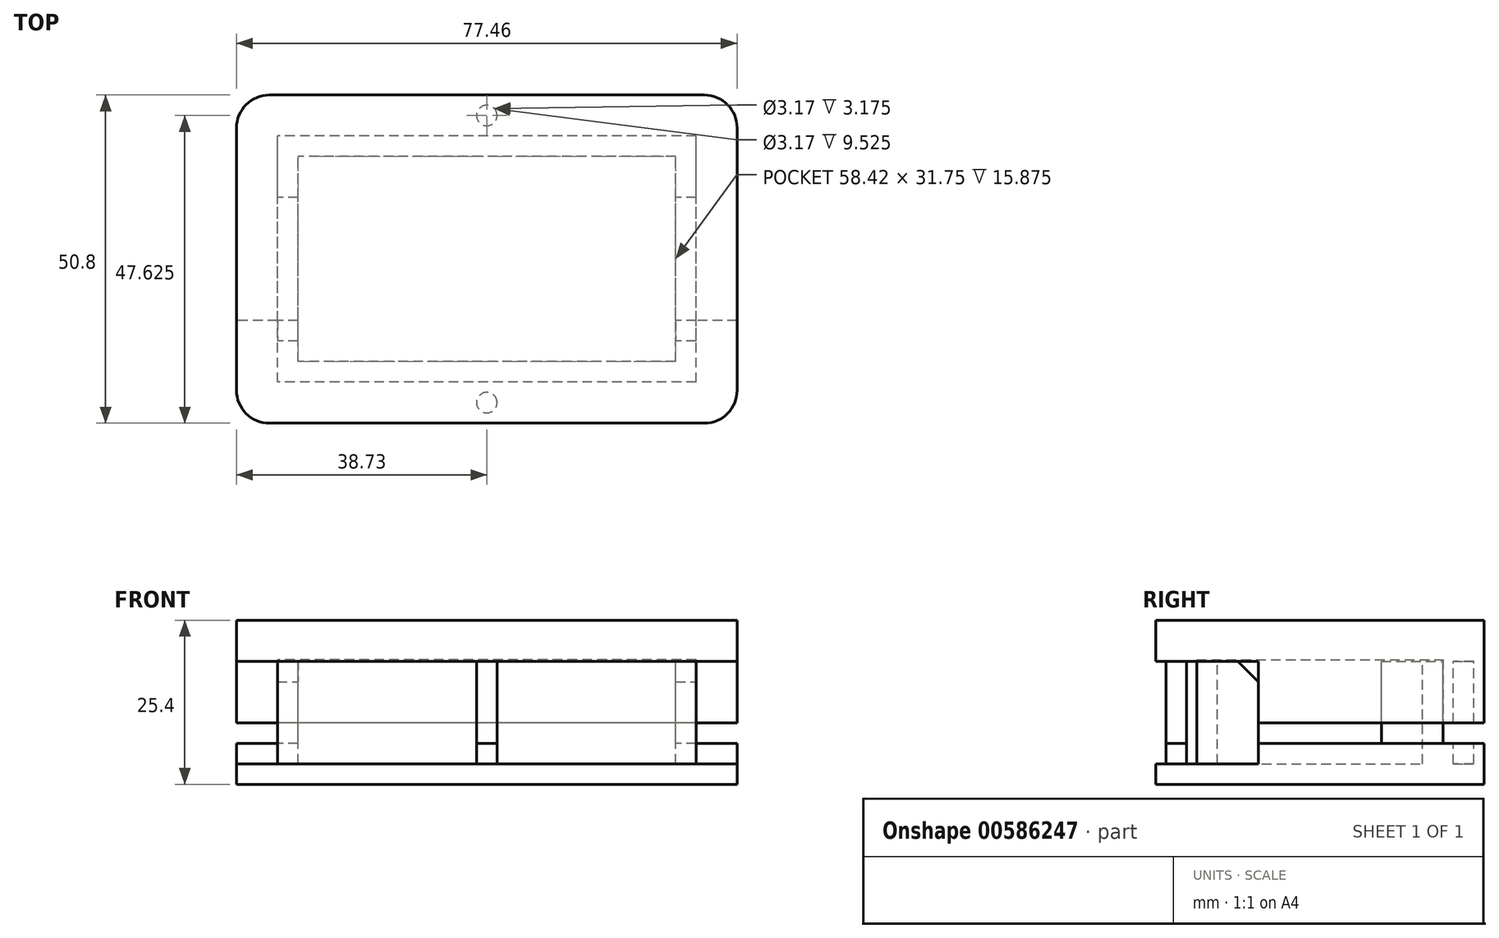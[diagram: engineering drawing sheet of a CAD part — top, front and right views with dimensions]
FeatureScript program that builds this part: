
annotation { "Feature Type Name" : "Feature", "Feature Type Description" : "" }
export const myFeature = defineFeature(function(context is Context, id is Id, definition is map)
    precondition{}
    {
        {
            var Q0;
            Q0=qCreatedBy(makeId("Top.planeOp"),FACE);
            var sketch = newSketch(context, id + "F0", { "sketchPlane" : qUnion([Q0])});
            skLineSegment(sketch, "E0.bottom", {"start": v(38.73, -25.4) * mm, "end": v(-38.73, -25.4) * mm});
            skLineSegment(sketch, "E0.top", {"start": v(38.73, 25.4) * mm, "end": v(-38.73, 25.4) * mm});
            skLineSegment(sketch, "E0.left", {"start": v(38.73, -25.4) * mm, "end": v(38.73, 25.4) * mm});
            skLineSegment(sketch, "E0.right", {"start": v(-38.73, -25.4) * mm, "end": v(-38.73, 25.4) * mm});
            skPoint(sketch, "E0.middle", {"position": v(0, 0) * mm});
            skSolve(sketch);
        }
        {
            var Q0;
            Q0 = qSketchRegion(id + "F0", true);
            extrude(context, id + "F1", {"entities" : qUnion([Q0]), "depth" : 19.05 * mm, "offsetDistance" : 25.4 * mm});
        }
        {
            var Q0;
            Q0=makeQuery(id+"F1.opExtrude","CAP_FACE",FACE,{"disambiguationData":[OSD([sQuery(id+"F0.wireOp",EDGE,"E0.bottom"),sQuery(id+"F0.wireOp",EDGE,"E0.top"),sQuery(id+"F0.wireOp",EDGE,"E0.left"),sQuery(id+"F0.wireOp",EDGE,"E0.right")])],"isStart":false});
            var sketch = newSketch(context, id + "F2", { "sketchPlane" : qUnion([Q0])});
            skLineSegment(sketch, "E1.bottom", {"start": v(29.21, -15.88) * mm, "end": v(-29.21, -15.88) * mm});
            skLineSegment(sketch, "E1.top", {"start": v(29.21, 15.88) * mm, "end": v(-29.21, 15.88) * mm});
            skLineSegment(sketch, "E1.left", {"start": v(29.21, -15.88) * mm, "end": v(29.21, 15.88) * mm});
            skLineSegment(sketch, "E1.right", {"start": v(-29.21, -15.88) * mm, "end": v(-29.21, 15.88) * mm});
            skPoint(sketch, "E1.middle", {"position": v(0, 0) * mm});
            skLineSegment(sketch, "E2.bottom", {"start": v(32.38, -19.05) * mm, "end": v(-32.38, -19.05) * mm});
            skLineSegment(sketch, "E2.top", {"start": v(32.38, 19.05) * mm, "end": v(-32.38, 19.05) * mm});
            skLineSegment(sketch, "E2.left", {"start": v(32.38, -19.05) * mm, "end": v(32.38, 19.05) * mm});
            skLineSegment(sketch, "E2.right", {"start": v(-32.38, -19.05) * mm, "end": v(-32.38, 19.05) * mm});
            skLineSegment(sketch, "E3.bottom", {"start": v(50.8, -9.53) * mm, "end": v(-50.8, -9.53) * mm});
            skLineSegment(sketch, "E3.top", {"start": v(50.8, 9.53) * mm, "end": v(-50.8, 9.53) * mm});
            skLineSegment(sketch, "E3.left", {"start": v(50.8, -9.53) * mm, "end": v(50.8, 9.53) * mm});
            skLineSegment(sketch, "E3.right", {"start": v(-50.8, -9.53) * mm, "end": v(-50.8, 9.53) * mm});
            skLineSegment(sketch, "E4", {"start": v(0, 25.4) * mm, "end": v(0, 19.05) * mm, "construction": true});
            skLineSegment(sketch, "E5", {"start": v(29.21, 0) * mm, "end": v(-29.21, 0) * mm, "construction": true});
            skCircle(sketch, "E6", {"center": v(0, 22.23) * mm, "radius": 1.59 * mm});
            skCircle(sketch, "E7.MirrorC", {"center": v(0, -22.23) * mm, "radius": 1.59 * mm});
            skSolve(sketch);
        }
        {
            var Q0;
            Q0=makeQuery(id+"F2.imprint","IMPRINT",FACE,{"disambiguationData":[TD([[makeQuery(id+"F2.imprint","IMPRINT",EDGE,{"derivedFrom":sQuery(id+"F2.wireOp",EDGE,"E1.bottom")}),-1.0]])]});
            var Q1;
            {var subQ0=sQuery(id+"F2.wireOp",EDGE,"E3.bottom");var subQ1=sQuery(id+"F2.wireOp",EDGE,"E1.left");var subQ2=makeQuery(id+"F2.imprint","INTERSECT",VERTEX,{"derivedFrom":[subQ1,subQ0]});Q1=makeQuery(id+"F2.imprint","IMPRINT",FACE,{"disambiguationData":[TD([[makeQuery(id+"F2.imprint","IMPRINT",EDGE,{"disambiguationData":[TD([[subQ2,-1.0]])],"derivedFrom":subQ1}),1.0]])]});}
            var Q2;
            {var subQ0=sQuery(id+"F2.wireOp",EDGE,"E1.top");Q2=makeQuery(id+"F2.imprint","IMPRINT",FACE,{"disambiguationData":[TD([[makeQuery(id+"F2.imprint","IMPRINT",EDGE,{"derivedFrom":subQ0}),1.0]])]});}
            extrude(context, id + "F3", {"entities" : qUnion([Q0, Q1, Q2]), "operationType" : NewBodyOperationType.REMOVE, "oppositeDirection" : true, "depth" : 15.88 * mm, "offsetDistance" : 25.4 * mm});
        }
        {
            var Q0;
            Q0=makeQuery(id+"F2.imprint","IMPRINT",FACE,{"disambiguationData":[TD([[makeQuery(id+"F2.imprint","IMPRINT",EDGE,{"derivedFrom":sQuery(id+"F2.wireOp",EDGE,"E2.bottom")}),1.0]])]});
            var Q1;
            {var subQ0=sQuery(id+"F2.wireOp",EDGE,"E3.bottom");var subQ1=sQuery(id+"F2.wireOp",EDGE,"E2.right");var subQ2=makeQuery(id+"F2.imprint","INTERSECT",VERTEX,{"derivedFrom":[subQ1,subQ0]});Q1=makeQuery(id+"F2.imprint","IMPRINT",FACE,{"disambiguationData":[TD([[makeQuery(id+"F2.imprint","IMPRINT",EDGE,{"disambiguationData":[TD([[subQ2,-1.0]])],"derivedFrom":subQ1}),1.0]])]});}
            var Q2;
            {var subQ0=sQuery(id+"F2.wireOp",EDGE,"E3.bottom");var subQ1=sQuery(id+"F2.wireOp",EDGE,"E2.left");var subQ2=makeQuery(id+"F2.imprint","INTERSECT",VERTEX,{"derivedFrom":[subQ1,subQ0]});Q2=makeQuery(id+"F2.imprint","IMPRINT",FACE,{"disambiguationData":[TD([[makeQuery(id+"F2.imprint","IMPRINT",EDGE,{"disambiguationData":[TD([[subQ2,-1.0]])],"derivedFrom":subQ1}),-1.0]])]});}
            var Q3;
            Q3=makeQuery(id+"F2.imprint","IMPRINT",FACE,{"disambiguationData":[TD([[makeQuery(id+"F2.imprint","IMPRINT",EDGE,{"derivedFrom":sQuery(id+"F2.wireOp",EDGE,"E6")}),1.0]])]});
            var Q4;
            {var subQ1=sQuery(id+"F2.wireOp",EDGE,"E2.top");Q4=makeQuery(id+"F2.imprint","IMPRINT",FACE,{"disambiguationData":[TD([[makeQuery(id+"F2.imprint","IMPRINT",EDGE,{"derivedFrom":subQ1}),-1.0]])]});}
            var Q5;
            Q5=makeQuery(id+"F2.imprint","IMPRINT",FACE,{"disambiguationData":[TD([[makeQuery(id+"F2.imprint","IMPRINT",EDGE,{"derivedFrom":sQuery(id+"F2.wireOp",EDGE,"E7.MirrorC")}),-1.0]])]});
            extrude(context, id + "F4", {"entities" : qUnion([Q0, Q1, Q2, Q3, Q4, Q5]), "operationType" : NewBodyOperationType.REMOVE, "oppositeDirection" : true, "depth" : 12.7 * mm, "offsetDistance" : 25.4 * mm});
        }
        {
            var Q0;
            {var subQ0=sQuery(id+"F2.wireOp",EDGE,"E3.bottom");var subQ1=sQuery(id+"F2.wireOp",EDGE,"E2.right");var subQ2=makeQuery(id+"F2.imprint","INTERSECT",VERTEX,{"derivedFrom":[subQ1,subQ0]});Q0=makeQuery(id+"F2.imprint","IMPRINT",FACE,{"disambiguationData":[TD([[makeQuery(id+"F2.imprint","IMPRINT",EDGE,{"disambiguationData":[TD([[subQ2,-1.0]])],"derivedFrom":subQ1}),1.0]])]});}
            var Q1;
            {var subQ0=sQuery(id+"F2.wireOp",EDGE,"E3.bottom");var subQ1=sQuery(id+"F2.wireOp",EDGE,"E1.right");var subQ2=makeQuery(id+"F2.imprint","INTERSECT",VERTEX,{"derivedFrom":[subQ1,subQ0]});Q1=makeQuery(id+"F2.imprint","IMPRINT",FACE,{"disambiguationData":[TD([[makeQuery(id+"F2.imprint","IMPRINT",EDGE,{"disambiguationData":[TD([[subQ2,-1.0]])],"derivedFrom":subQ1}),1.0]])]});}
            var Q2;
            {var subQ0=sQuery(id+"F2.wireOp",EDGE,"E3.bottom");var subQ1=sQuery(id+"F2.wireOp",EDGE,"E1.left");var subQ2=makeQuery(id+"F2.imprint","INTERSECT",VERTEX,{"derivedFrom":[subQ1,subQ0]});Q2=makeQuery(id+"F2.imprint","IMPRINT",FACE,{"disambiguationData":[TD([[makeQuery(id+"F2.imprint","IMPRINT",EDGE,{"disambiguationData":[TD([[subQ2,-1.0]])],"derivedFrom":subQ1}),-1.0]])]});}
            var Q3;
            {var subQ0=sQuery(id+"F2.wireOp",EDGE,"E3.bottom");var subQ1=sQuery(id+"F2.wireOp",EDGE,"E2.left");var subQ2=makeQuery(id+"F2.imprint","INTERSECT",VERTEX,{"derivedFrom":[subQ1,subQ0]});Q3=makeQuery(id+"F2.imprint","IMPRINT",FACE,{"disambiguationData":[TD([[makeQuery(id+"F2.imprint","IMPRINT",EDGE,{"disambiguationData":[TD([[subQ2,-1.0]])],"derivedFrom":subQ1}),-1.0]])]});}
            var Q4;
            Q4=makeQuery(id+"F3.boolean.opBoolean","COPY",FACE,{"derivedFrom":makeQuery(id+"F3.opExtrude","CAP_FACE",FACE,{"disambiguationData":[OSD([sQuery(id+"F2.wireOp",EDGE,"E1.bottom"),sQuery(id+"F2.wireOp",EDGE,"E1.top"),sQuery(id+"F2.wireOp",EDGE,"E1.left"),sQuery(id+"F2.wireOp",EDGE,"E1.right")])],"isStart":false})});
            extrude(context, id + "F5", {"entities" : qUnion([Q0, Q1, Q2, Q3]), "operationType" : NewBodyOperationType.REMOVE, "oppositeDirection" : true, "depth" : 12.7 * mm, "endBoundEntityFace" : qUnion([Q4]), "offsetDistance" : 25.4 * mm});
        }
        {
            var Q0;
            {var subQ0=sQuery(id+"F2.wireOp",EDGE,"E3.top");var subQ1=makeQuery(id+"F2.imprint","INTERSECT",VERTEX,{"derivedFrom":[sQuery(id+"F2.wireOp",EDGE,"E2.right"),subQ0]});Q0=makeQuery(id+"F5.boolean.opBoolean","COPY",EDGE,{"derivedFrom":makeQuery(id+"F5.opExtrude","CAP_EDGE",EDGE,{"disambiguationData":[OSD([subQ0]),TDD([makeQuery(id+"F2.imprint","IMPRINT",EDGE,{"disambiguationData":[TD([[makeQuery(id+"F2.imprint","INTERSECT",VERTEX,{"derivedFrom":[sQuery(id+"F2.wireOp",EDGE,"E1.right"),subQ0]}),-1.0]])],"derivedFrom":subQ0}),makeQuery(id+"F2.imprint","IMPRINT",EDGE,{"disambiguationData":[TD([[subQ1,-1.0]])],"derivedFrom":subQ0})])],"isStart":true})});}
            var Q1;
            {var subQ0=sQuery(id+"F2.wireOp",EDGE,"E3.bottom");var subQ1=makeQuery(id+"F2.imprint","INTERSECT",VERTEX,{"derivedFrom":[sQuery(id+"F2.wireOp",EDGE,"E2.right"),subQ0]});Q1=makeQuery(id+"F5.boolean.opBoolean","COPY",EDGE,{"derivedFrom":makeQuery(id+"F5.opExtrude","CAP_EDGE",EDGE,{"disambiguationData":[OSD([subQ0]),TDD([makeQuery(id+"F2.imprint","IMPRINT",EDGE,{"disambiguationData":[TD([[makeQuery(id+"F2.imprint","INTERSECT",VERTEX,{"derivedFrom":[sQuery(id+"F2.wireOp",EDGE,"E1.right"),subQ0]}),-1.0]])],"derivedFrom":subQ0}),makeQuery(id+"F2.imprint","IMPRINT",EDGE,{"disambiguationData":[TD([[subQ1,-1.0]])],"derivedFrom":subQ0})])],"isStart":true})});}
            var Q2;
            {var subQ0=sQuery(id+"F2.wireOp",EDGE,"E3.top");var subQ1=makeQuery(id+"F2.imprint","INTERSECT",VERTEX,{"derivedFrom":[sQuery(id+"F2.wireOp",EDGE,"E2.left"),subQ0]});Q2=makeQuery(id+"F5.boolean.opBoolean","COPY",EDGE,{"derivedFrom":makeQuery(id+"F5.opExtrude","CAP_EDGE",EDGE,{"disambiguationData":[OSD([subQ0]),TDD([makeQuery(id+"F2.imprint","IMPRINT",EDGE,{"disambiguationData":[TD([[subQ1,1.0]])],"derivedFrom":subQ0}),makeQuery(id+"F2.imprint","IMPRINT",EDGE,{"disambiguationData":[TD([[makeQuery(id+"F2.imprint","INTERSECT",VERTEX,{"derivedFrom":[sQuery(id+"F2.wireOp",EDGE,"E1.left"),subQ0]}),1.0]])],"derivedFrom":subQ0})])],"isStart":true})});}
            var Q3;
            {var subQ0=sQuery(id+"F2.wireOp",EDGE,"E3.bottom");var subQ1=makeQuery(id+"F2.imprint","INTERSECT",VERTEX,{"derivedFrom":[sQuery(id+"F2.wireOp",EDGE,"E2.left"),subQ0]});Q3=makeQuery(id+"F5.boolean.opBoolean","COPY",EDGE,{"derivedFrom":makeQuery(id+"F5.opExtrude","CAP_EDGE",EDGE,{"disambiguationData":[OSD([subQ0]),TDD([makeQuery(id+"F2.imprint","IMPRINT",EDGE,{"disambiguationData":[TD([[subQ1,1.0]])],"derivedFrom":subQ0}),makeQuery(id+"F2.imprint","IMPRINT",EDGE,{"disambiguationData":[TD([[makeQuery(id+"F2.imprint","INTERSECT",VERTEX,{"derivedFrom":[sQuery(id+"F2.wireOp",EDGE,"E1.left"),subQ0]}),1.0]])],"derivedFrom":subQ0})])],"isStart":true})});}
            chamfer(context, id + "F6", {"entities" : qUnion([Q0, Q1, Q2, Q3]), "width" : 3.17 * mm, "tangentPropagation" : true});
        }
        {
            var Q0;
            {var subQ0=sQuery(id+"F2.wireOp",EDGE,"E3.top");var subQ1=sQuery(id+"F2.wireOp",EDGE,"E3.bottom");var subQ2=sQuery(id+"F0.wireOp",EDGE,"E0.right");var subQ3=sQuery(id+"F0.wireOp",EDGE,"E0.left");Q0=makeQuery(id+"F5.boolean.opBoolean","MERGE",FACE,{"derivedFrom":[makeQuery(id+"F4.boolean.opBoolean","COPY",FACE,{"derivedFrom":makeQuery(id+"F4.opExtrude","CAP_FACE",FACE,{"disambiguationData":[OSD([sQuery(id+"F0.wireOp",EDGE,"E0.bottom"),sQuery(id+"F0.wireOp",EDGE,"E0.top"),subQ3,subQ2,sQuery(id+"F2.wireOp",EDGE,"E2.bottom"),sQuery(id+"F2.wireOp",EDGE,"E2.top"),sQuery(id+"F2.wireOp",EDGE,"E2.left"),sQuery(id+"F2.wireOp",EDGE,"E2.right")])],"isStart":false})}),makeQuery(id+"F5.opExtrude","CAP_FACE",FACE,{"disambiguationData":[OSD([subQ3,sQuery(id+"F2.wireOp",EDGE,"E1.left"),subQ1,subQ0])],"isStart":false}),makeQuery(id+"F5.opExtrude","CAP_FACE",FACE,{"disambiguationData":[OSD([subQ2,sQuery(id+"F2.wireOp",EDGE,"E1.right"),subQ1,subQ0])],"isStart":false})]});}
            var sketch = newSketch(context, id + "F7", { "sketchPlane" : qUnion([Q0])});
            skLineSegment(sketch, "E8.0", {"start": v(38.73, -25.4) * mm, "end": v(-38.73, -25.4) * mm});
            skLineSegment(sketch, "E9.0", {"start": v(38.73, -25.4) * mm, "end": v(38.73, 25.4) * mm});
            skLineSegment(sketch, "E10.0", {"start": v(38.73, 25.4) * mm, "end": v(-38.73, 25.4) * mm});
            skLineSegment(sketch, "E11.0", {"start": v(-38.73, -25.4) * mm, "end": v(-38.73, 25.4) * mm});
            skLineSegment(sketch, "E12.bottom", {"start": v(-32.38, -19.05) * mm, "end": v(32.38, -19.05) * mm});
            skLineSegment(sketch, "E12.top", {"start": v(-32.38, 19.05) * mm, "end": v(32.38, 19.05) * mm});
            skLineSegment(sketch, "E12.left", {"start": v(-32.38, -19.05) * mm, "end": v(-32.38, 19.05) * mm});
            skLineSegment(sketch, "E12.right", {"start": v(32.38, -19.05) * mm, "end": v(32.38, 19.05) * mm});
            skSolve(sketch);
        }
        {
            var Q0;
            Q0 = qSketchRegion(id + "F7", true);
            extrude(context, id + "F8", {"entities" : qUnion([Q0]), "depth" : 19.05 * mm, "offsetDistance" : 25.4 * mm});
        }
        {
            var Q0;
            Q0=makeQuery(id+"F8.opExtrude","CAP_FACE",FACE,{"disambiguationData":[OSD([sQuery(id+"F7.wireOp",EDGE,"E8.0"),sQuery(id+"F7.wireOp",EDGE,"E9.0"),sQuery(id+"F7.wireOp",EDGE,"E10.0"),sQuery(id+"F7.wireOp",EDGE,"E11.0"),sQuery(id+"F7.wireOp",EDGE,"E12.bottom"),sQuery(id+"F7.wireOp",EDGE,"E12.top"),sQuery(id+"F7.wireOp",EDGE,"E12.left"),sQuery(id+"F7.wireOp",EDGE,"E12.right")])],"isStart":false});
            var sketch = newSketch(context, id + "F9", { "sketchPlane" : qUnion([Q0])});
            skLineSegment(sketch, "E13.bottom", {"start": v(-32.38, 19.05) * mm, "end": v(32.38, 19.05) * mm});
            skLineSegment(sketch, "E13.top", {"start": v(-32.38, -19.05) * mm, "end": v(32.38, -19.05) * mm});
            skLineSegment(sketch, "E13.left", {"start": v(-32.38, 19.05) * mm, "end": v(-32.38, -19.05) * mm});
            skLineSegment(sketch, "E13.right", {"start": v(32.38, 19.05) * mm, "end": v(32.38, -19.05) * mm});
            skSolve(sketch);
        }
        {
            var Q0;
            Q0=makeQuery(id+"F9.imprint","IMPRINT",FACE,{"disambiguationData":[TD([[makeQuery(id+"F9.imprint","IMPRINT",EDGE,{"derivedFrom":sQuery(id+"F9.wireOp",EDGE,"E13.bottom")}),1.0]])]});
            extrude(context, id + "F10", {"entities" : qUnion([Q0]), "operationType" : NewBodyOperationType.ADD, "oppositeDirection" : true, "depth" : 6.1 * mm, "offsetDistance" : 25.4 * mm});
        }
        {
            var Q0;
            Q0=makeQuery(id+"F8.opExtrude","SWEPT_EDGE",EDGE,{"disambiguationData":[OSD([sQuery(id+"F7.wireOp",EDGE,"E10.0"),sQuery(id+"F7.wireOp",EDGE,"E11.0")])]});
            var Q1;
            Q1=makeQuery(id+"F1.opExtrude","SWEPT_EDGE",EDGE,{"disambiguationData":[OSD([sQuery(id+"F0.wireOp",EDGE,"E0.top"),sQuery(id+"F0.wireOp",EDGE,"E0.right")])]});
            var Q2;
            Q2=makeQuery(id+"F8.opExtrude","SWEPT_EDGE",EDGE,{"disambiguationData":[OSD([sQuery(id+"F7.wireOp",EDGE,"E8.0"),sQuery(id+"F7.wireOp",EDGE,"E11.0")])]});
            var Q3;
            Q3=makeQuery(id+"F1.opExtrude","SWEPT_EDGE",EDGE,{"disambiguationData":[OSD([sQuery(id+"F0.wireOp",EDGE,"E0.bottom"),sQuery(id+"F0.wireOp",EDGE,"E0.right")])]});
            var Q4;
            Q4=makeQuery(id+"F8.opExtrude","SWEPT_EDGE",EDGE,{"disambiguationData":[OSD([sQuery(id+"F7.wireOp",EDGE,"E9.0"),sQuery(id+"F7.wireOp",EDGE,"E10.0")])]});
            var Q5;
            Q5=makeQuery(id+"F8.opExtrude","SWEPT_EDGE",EDGE,{"disambiguationData":[OSD([sQuery(id+"F7.wireOp",EDGE,"E8.0"),sQuery(id+"F7.wireOp",EDGE,"E9.0")])]});
            var Q6;
            Q6=makeQuery(id+"F1.opExtrude","SWEPT_EDGE",EDGE,{"disambiguationData":[OSD([sQuery(id+"F0.wireOp",EDGE,"E0.top"),sQuery(id+"F0.wireOp",EDGE,"E0.left")])]});
            var Q7;
            Q7=makeQuery(id+"F1.opExtrude","SWEPT_EDGE",EDGE,{"disambiguationData":[OSD([sQuery(id+"F0.wireOp",EDGE,"E0.bottom"),sQuery(id+"F0.wireOp",EDGE,"E0.left")])]});
            fillet(context, id + "F11", {"entities" : qUnion([Q0, Q1, Q2, Q3, Q4, Q5, Q6, Q7]), "radius" : 5.08 * mm, "tangentPropagation" : true, "allowEdgeOverflow" : false});
        }
        {
            var Q0;
            Q0=makeQuery(id+"F2.imprint","IMPRINT",FACE,{"disambiguationData":[TD([[makeQuery(id+"F2.imprint","IMPRINT",EDGE,{"derivedFrom":sQuery(id+"F2.wireOp",EDGE,"E6")}),1.0]])]});
            var Q1;
            Q1=makeQuery(id+"F2.imprint","IMPRINT",FACE,{"disambiguationData":[TD([[makeQuery(id+"F2.imprint","IMPRINT",EDGE,{"derivedFrom":sQuery(id+"F2.wireOp",EDGE,"E7.MirrorC")}),-1.0]])]});
            extrude(context, id + "F12", {"entities" : qUnion([Q0, Q1]), "operationType" : NewBodyOperationType.REMOVE, "oppositeDirection" : true, "depth" : 15.88 * mm, "offsetDistance" : 25.4 * mm});
        }
        {
            var Q0;
            Q0=makeQuery(id+"F4.boolean.opBoolean","COPY",EDGE,{"derivedFrom":makeQuery(id+"F4.opExtrude","CAP_EDGE",EDGE,{"disambiguationData":[OSD([sQuery(id+"F0.wireOp",EDGE,"E0.top")])],"isStart":false})});
            var Q1;
            Q1=makeQuery(id+"F8.opExtrude","CAP_EDGE",EDGE,{"disambiguationData":[OSD([sQuery(id+"F7.wireOp",EDGE,"E11.0")])],"isStart":true});
            var Q2;
            Q2=makeQuery(id+"F8.opExtrude","CAP_EDGE",EDGE,{"disambiguationData":[OSD([sQuery(id+"F7.wireOp",EDGE,"E12.top")])],"isStart":true});
            var Q3;
            Q3=makeQuery(id+"F8.opExtrude","CAP_EDGE",EDGE,{"disambiguationData":[OSD([sQuery(id+"F7.wireOp",EDGE,"E12.left")])],"isStart":true});
            var Q4;
            Q4=makeQuery(id+"F8.opExtrude","CAP_EDGE",EDGE,{"disambiguationData":[OSD([sQuery(id+"F7.wireOp",EDGE,"E12.bottom")])],"isStart":true});
            var Q5;
            Q5=makeQuery(id+"F8.opExtrude","CAP_EDGE",EDGE,{"disambiguationData":[OSD([sQuery(id+"F7.wireOp",EDGE,"E12.right")])],"isStart":true});
            chamfer(context, id + "F13", {"entities" : qUnion([Q0, Q1, Q2, Q3, Q4, Q5]), "width" : 1.59 * mm, "tangentPropagation" : true});
        }
        {
            var Q0;
            Q0=makeQuery(id+"F7.imprint","IMPRINT",FACE,{"disambiguationData":[TD([[makeQuery(id+"F7.imprint","IMPRINT",EDGE,{"derivedFrom":sQuery(id+"F7.wireOp",EDGE,"E8.0")}),-1.0]])]});
            var sketch = newSketch(context, id + "F14", { "sketchPlane" : qUnion([Q0])});
            skCircle(sketch, "E14.0", {"center": v(0, 22.23) * mm, "radius": 1.59 * mm});
            skCircle(sketch, "E15.0", {"center": v(0, -22.23) * mm, "radius": 1.59 * mm});
            skSolve(sketch);
        }
        {
            var Q0;
            Q0=makeQuery(id+"F14.imprint","IMPRINT",FACE,{"disambiguationData":[TD([[makeQuery(id+"F14.imprint","IMPRINT",EDGE,{"derivedFrom":sQuery(id+"F14.wireOp",EDGE,"E14.0")}),1.0]])]});
            var Q1;
            Q1=makeQuery(id+"F14.imprint","IMPRINT",FACE,{"disambiguationData":[TD([[makeQuery(id+"F14.imprint","IMPRINT",EDGE,{"derivedFrom":sQuery(id+"F14.wireOp",EDGE,"E15.0")}),-1.0]])]});
            extrude(context, id + "F15", {"entities" : qUnion([Q0, Q1]), "operationType" : NewBodyOperationType.REMOVE, "depth" : 3.17 * mm, "offsetDistance" : 25.4 * mm});
        }
    });
